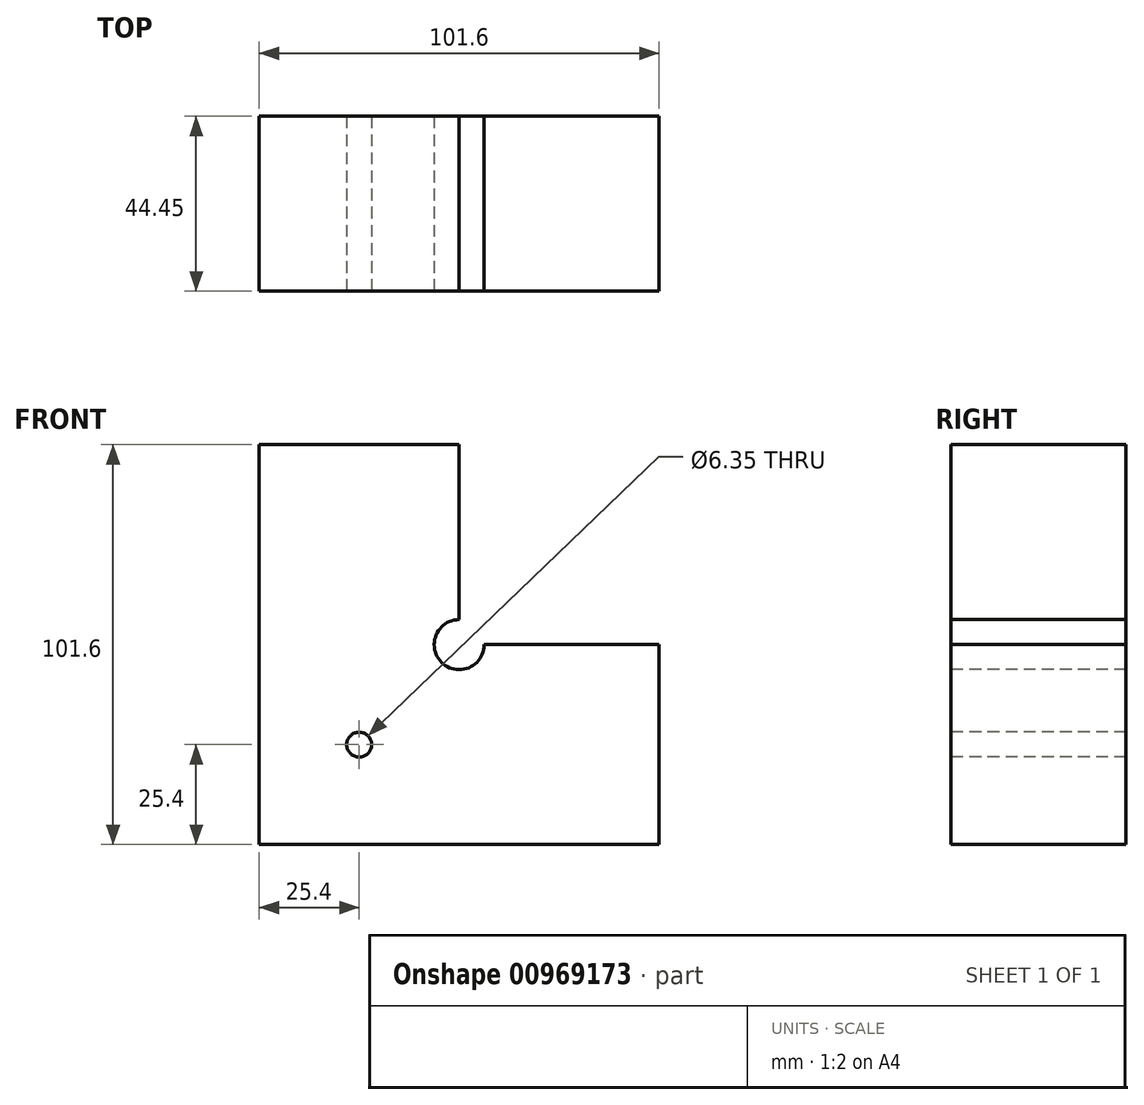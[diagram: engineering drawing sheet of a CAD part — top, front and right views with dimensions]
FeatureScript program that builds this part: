
annotation { "Feature Type Name" : "Feature", "Feature Type Description" : "" }
export const myFeature = defineFeature(function(context is Context, id is Id, definition is map)
    precondition{}
    {
        {
            var Q0;
            Q0=qCreatedBy(makeId("Front.planeOp"),FACE);
            var sketch = newSketch(context, id + "F0", { "sketchPlane" : qUnion([Q0])});
            skLineSegment(sketch, "E0.bottom", {"start": v(50.8, -50.8) * mm, "end": v(-50.8, -50.8) * mm});
            skLineSegment(sketch, "E0.top", {"start": v(50.8, 50.8) * mm, "end": v(-50.8, 50.8) * mm});
            skLineSegment(sketch, "E0.left", {"start": v(50.8, -50.8) * mm, "end": v(50.8, 50.8) * mm});
            skLineSegment(sketch, "E0.right", {"start": v(-50.8, -50.8) * mm, "end": v(-50.8, 50.8) * mm});
            skPoint(sketch, "E0.middle", {"position": v(0, 0) * mm});
            skSolve(sketch);
        }
        {
            var Q0;
            Q0 = qSketchRegion(id + "F0", true);
            extrude(context, id + "F1", {"entities" : qUnion([Q0]), "depth" : 44.45 * mm, "offsetDistance" : 25.4 * mm});
        }
        {
            var Q0;
            Q0=makeQuery(id+"F1.opExtrude","CAP_FACE",FACE,{"disambiguationData":[OSD([sQuery(id+"F0.wireOp",EDGE,"E0.bottom"),sQuery(id+"F0.wireOp",EDGE,"E0.top"),sQuery(id+"F0.wireOp",EDGE,"E0.left"),sQuery(id+"F0.wireOp",EDGE,"E0.right")])],"isStart":false});
            var sketch = newSketch(context, id + "F2", { "sketchPlane" : qUnion([Q0])});
            skPoint(sketch, "E1", {"position": v(0, 0) * mm});
            skSolve(sketch);
        }
        {
            var Q0;
            Q0=sQuery(id+"F2.wireOp",VERTEX,"E1");
            var Q1;
            Q1=makeQuery(id+"F1.opExtrude","SWEPT_BODY",BODY,{"disambiguationData":[OSD([sQuery(id+"F0.wireOp",EDGE,"E0.bottom"),sQuery(id+"F0.wireOp",EDGE,"E0.top"),sQuery(id+"F0.wireOp",EDGE,"E0.left"),sQuery(id+"F0.wireOp",EDGE,"E0.right")])]});
            hole(context, id + "F3", {"style" : HoleStyle.SIMPLE, "endStyle" : HoleEndStyle.THROUGH, "holeDiameter" : 12.7 * mm, "majorDiameter" : 6.35 * mm, "isTappedThrough" : true, "tappedDepth" : 12.7 * mm, "tapClearance" : 3, "locations" : qUnion([Q0]), "scope" : qUnion([Q1])});
        }
        {
            var Q0;
            Q0=makeQuery(id+"F1.opExtrude","CAP_FACE",FACE,{"disambiguationData":[OSD([sQuery(id+"F0.wireOp",EDGE,"E0.bottom"),sQuery(id+"F0.wireOp",EDGE,"E0.top"),sQuery(id+"F0.wireOp",EDGE,"E0.left"),sQuery(id+"F0.wireOp",EDGE,"E0.right")])],"isStart":false});
            var sketch = newSketch(context, id + "F4", { "sketchPlane" : qUnion([Q0])});
            skLineSegment(sketch, "E2", {"start": v(0, 50.8) * mm, "end": v(0, 0) * mm});
            skLineSegment(sketch, "E3", {"start": v(0, 0) * mm, "end": v(50.8, 0) * mm});
            skSolve(sketch);
        }
        {
            var Q0;
            Q0 = qSketchRegion(id + "F4", true);
            var Q1;
            {var subQ0=makeQuery(id+"F1.opExtrude","CAP_EDGE",EDGE,{"disambiguationData":[OSD([sQuery(id+"F0.wireOp",EDGE,"E0.left")])],"isStart":false});var subQ1=makeQuery(id+"F1.opExtrude","CAP_EDGE",EDGE,{"disambiguationData":[OSD([sQuery(id+"F0.wireOp",EDGE,"E0.top")])],"isStart":false});var subQ2=makeQuery(id+"F4.imprint","INTERSECT",VERTEX,{"derivedFrom":[subQ1,subQ0]});Q1=makeQuery(id+"F4.imprint","IMPRINT",FACE,{"disambiguationData":[TD([[makeQuery(id+"F4.imprint","IMPRINT",EDGE,{"disambiguationData":[TD([[subQ2,-1.0]])],"derivedFrom":subQ1}),1.0]])]});}
            extrude(context, id + "F5", {"entities" : qUnion([Q0, Q1]), "operationType" : NewBodyOperationType.REMOVE, "oppositeDirection" : true, "depth" : 88.9 * mm, "offsetDistance" : 25.4 * mm});
        }
        {
            var Q0;
            Q0=makeQuery(id+"F1.opExtrude","CAP_FACE",FACE,{"disambiguationData":[OSD([sQuery(id+"F0.wireOp",EDGE,"E0.bottom"),sQuery(id+"F0.wireOp",EDGE,"E0.top"),sQuery(id+"F0.wireOp",EDGE,"E0.left"),sQuery(id+"F0.wireOp",EDGE,"E0.right")])],"isStart":false});
            var sketch = newSketch(context, id + "F6", { "sketchPlane" : qUnion([Q0])});
            skLineSegment(sketch, "E4", {"start": v(-25.4, 50.8) * mm, "end": v(-25.4, -50.8) * mm, "construction": true});
            skLineSegment(sketch, "E5", {"start": v(50.8, -25.4) * mm, "end": v(-50.8, -25.4) * mm, "construction": true});
            skPoint(sketch, "E6", {"position": v(-25.4, -25.4) * mm});
            skSolve(sketch);
        }
        {
            var Q0;
            Q0=sQuery(id+"F6.wireOp",VERTEX,"E6");
            var Q1;
            Q1=makeQuery(id+"F1.opExtrude","SWEPT_BODY",BODY,{"disambiguationData":[OSD([sQuery(id+"F0.wireOp",EDGE,"E0.bottom"),sQuery(id+"F0.wireOp",EDGE,"E0.top"),sQuery(id+"F0.wireOp",EDGE,"E0.left"),sQuery(id+"F0.wireOp",EDGE,"E0.right")])]});
            hole(context, id + "F7", {"style" : HoleStyle.SIMPLE, "endStyle" : HoleEndStyle.THROUGH, "holeDiameter" : 6.35 * mm, "majorDiameter" : 6.35 * mm, "isTappedThrough" : true, "tappedDepth" : 12.7 * mm, "tapClearance" : 3, "locations" : qUnion([Q0]), "scope" : qUnion([Q1])});
        }
    });
